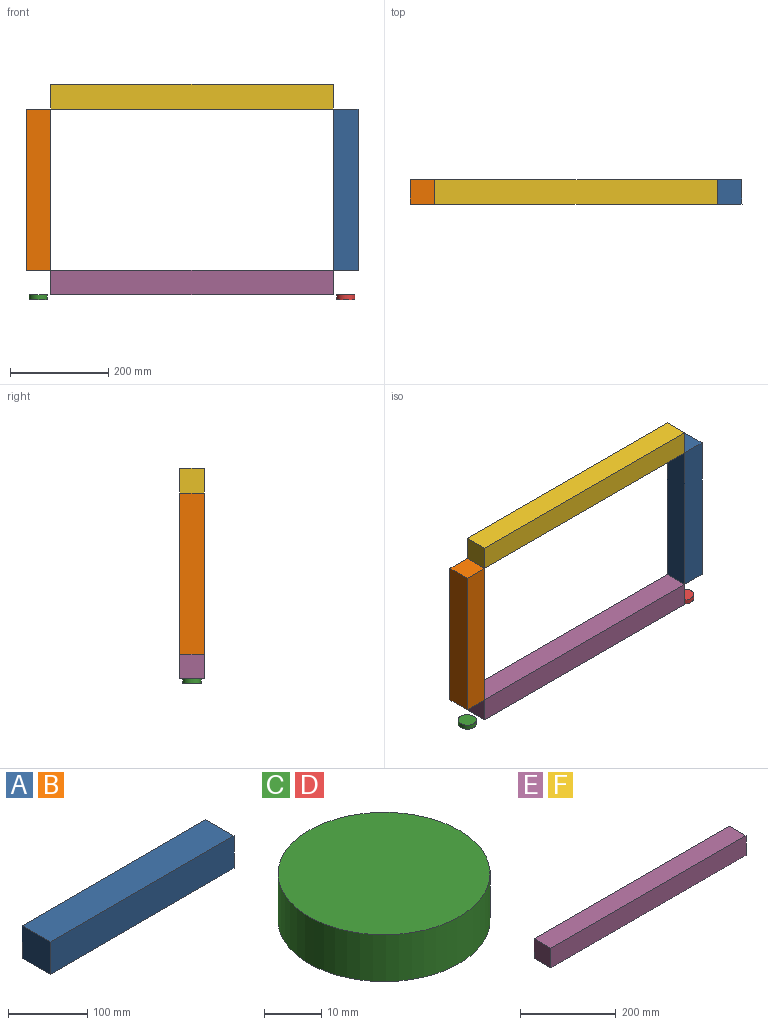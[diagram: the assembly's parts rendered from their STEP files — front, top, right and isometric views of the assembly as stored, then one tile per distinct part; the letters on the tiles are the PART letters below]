
ASSEMBLY  parts=6 mates=13
PART A: 6 faces, bbox 328x50x50 mm
  f0: plane 328x50mm, normal (0,1,0), area 16400mm2, adj f1,f3,f4,f5
  f1: plane 50x50mm, normal (-1,0,0), area 2500mm2, adj f0,f2,f4,f5
  f2: plane 328x50mm, normal (0,-1,0), area 16400mm2, adj f1,f3,f4,f5
  f3: plane 50x50mm, normal (1,0,0), area 2500mm2, adj f0,f2,f4,f5
  f4: plane 328x50mm, normal (0,0,1), area 16400mm2, adj f0,f1,f2,f3
  f5: plane 328x50mm, normal (0,0,-1), area 16400mm2, adj f0,f1,f2,f3
PART B: same geometry as A
PART C: 3 faces, bbox 37x37x10 mm
  f0: cylinder r=18.5mm len=37mm, axis (0,0,-1), area 1162.4mm2, adj f1,f2
  f1: plane 37x37mm, normal (0,0,1), area 1075.2mm2, adj f0
  f2: plane 37x37mm, normal (0,0,-1), area 1075.2mm2, adj f0
PART D: same geometry as C
PART E: 6 faces, bbox 576x50x50 mm
  f0: plane 576x50mm, normal (0,1,0), area 28800mm2, adj f1,f3,f4,f5
  f1: plane 50x50mm, normal (-1,0,0), area 2500mm2, adj f0,f2,f4,f5
  f2: plane 576x50mm, normal (0,-1,0), area 28800mm2, adj f1,f3,f4,f5
  f3: plane 50x50mm, normal (1,0,0), area 2500mm2, adj f0,f2,f4,f5
  f4: plane 576x50mm, normal (0,0,1), area 28800mm2, adj f0,f1,f2,f3
  f5: plane 576x50mm, normal (0,0,-1), area 28800mm2, adj f0,f1,f2,f3
PART F: same geometry as E
PLACE A rot(axis=(0.71,0,-0.71),180deg) t=(540.61,270.43,480.05)mm
PLACE B rot(axis=(-0.58,0.58,0.58),120deg) t=(102.53,32.5,480.05)mm
PLACE C rot(axis=(-1,0,0),180deg) t=(-110.39,-1742.15,102.05)mm
PLACE D t=(515.61,1857.14,92.05)mm
PLACE E t=(-85.39,-52.63,102.05)mm
PLACE F t=(-85.39,-52.63,480.05)mm
MATE planar C.f0 <-> E.f5  axis (0,0,1) through (-110.39,57.5,102.05)mm
MATE planar B.f3 <-> E.f4  axis (0,0,-1) through (-110.39,57.5,152.05)mm
MATE cylindrical C.f0 <-> B.f3  axis (0,0,1) through (-110.39,57.5,102.05)mm
MATE planar F.f5 <-> B.f1  axis (0,0,-1) through (202.61,57.5,480.05)mm
MATE planar E.f5 <-> D.f0  axis (0,0,-1) through (202.61,57.5,102.05)mm
MATE planar B.f2 <-> E.f1  axis (1,0,0) through (-85.39,57.5,316.05)mm
MATE planar A.f1 <-> F.f5  axis (0,0,1) through (515.61,57.5,480.05)mm
MATE planar A.f0 <-> F.f2  axis (0,-1,0) through (515.61,32.5,316.05)mm
MATE planar B.f2 <-> F.f1  axis (1,0,0) through (-85.39,57.5,316.05)mm
MATE planar B.f5 <-> E.f2  axis (0,-1,0) through (-110.39,32.5,316.05)mm
MATE planar A.f4 <-> E.f3  axis (-1,0,0) through (490.61,57.5,316.05)mm
MATE cylindrical D.f0 <-> A.f3  axis (0,0,1) through (515.61,57.5,102.05)mm
MATE planar B.f5 <-> F.f2  axis (0,-1,0) through (-110.39,32.5,316.05)mm
